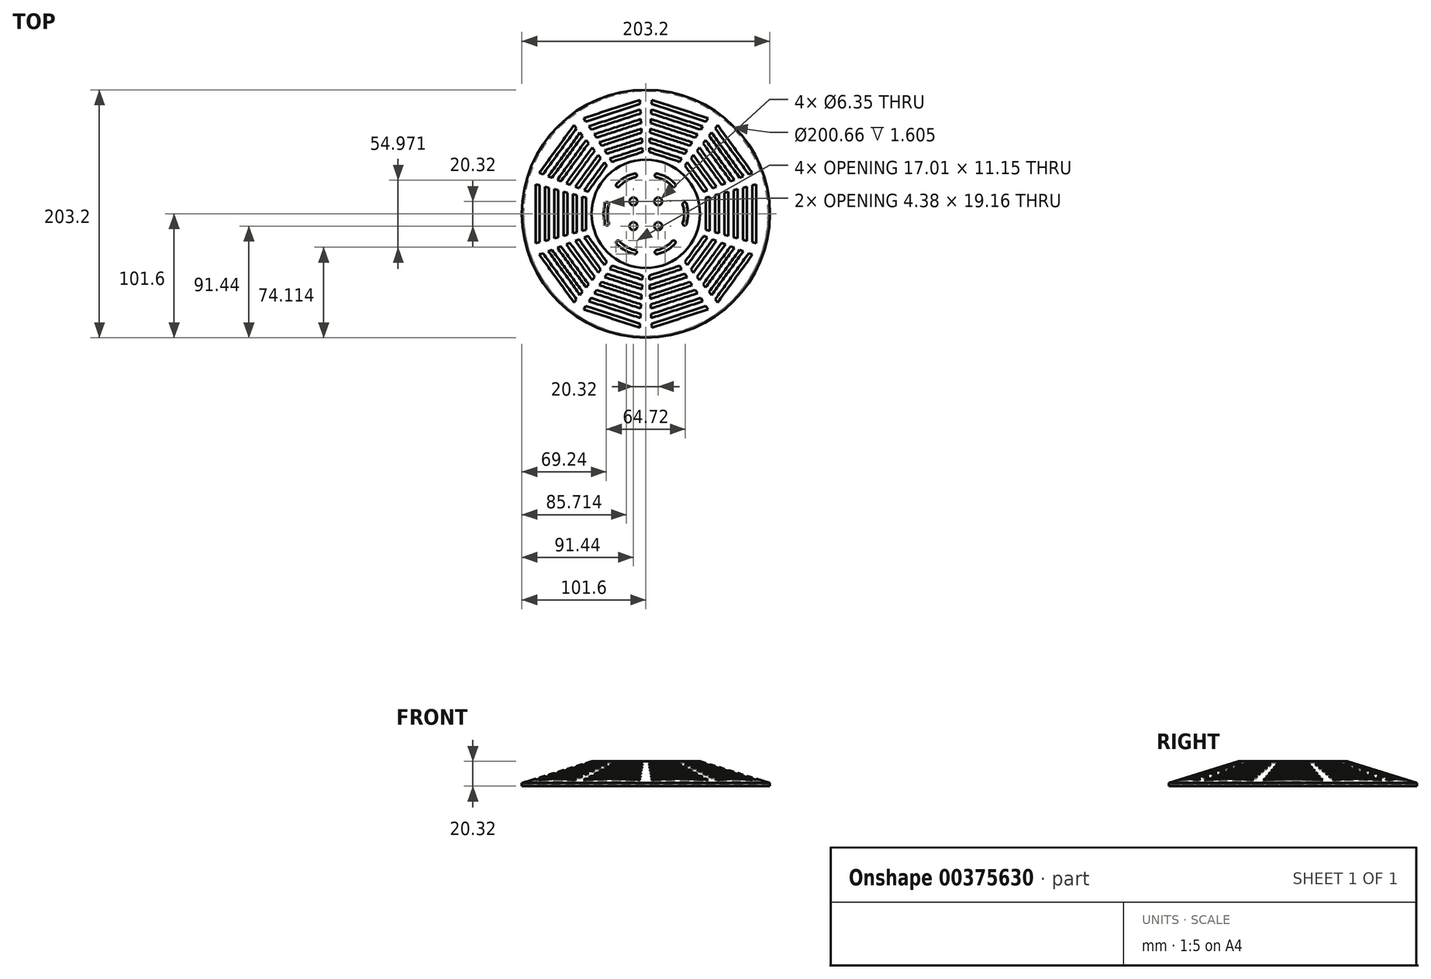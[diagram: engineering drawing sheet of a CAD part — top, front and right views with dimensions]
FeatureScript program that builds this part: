
annotation { "Feature Type Name" : "Feature", "Feature Type Description" : "" }
export const myFeature = defineFeature(function(context is Context, id is Id, definition is map)
    precondition{}
    {
        {
            var Q0;
            Q0=qCreatedBy(makeId("Front.planeOp"),FACE);
            var sketch = newSketch(context, id + "F0", { "sketchPlane" : qUnion([Q0])});
            skLineSegment(sketch, "E0", {"start": v(0, 0) * mm, "end": v(0, 20.32) * mm});
            skLineSegment(sketch, "E1", {"start": v(0, 20.32) * mm, "end": v(44.45, 20.32) * mm});
            skLineSegment(sketch, "E2", {"start": v(44.45, 20.32) * mm, "end": v(101.6, 2.54) * mm});
            skLineSegment(sketch, "E3", {"start": v(101.6, 2.54) * mm, "end": v(101.6, 0) * mm});
            skLineSegment(sketch, "E4", {"start": v(101.6, 0) * mm, "end": v(0, 0) * mm});
            skSolve(sketch);
        }
        {
            var Q0;
            Q0=makeQuery(id+"F0.imprint","IMPRINT",FACE,{"disambiguationData":[TD([[makeQuery(id+"F0.imprint","IMPRINT",EDGE,{"derivedFrom":sQuery(id+"F0.wireOp",EDGE,"E0")}),-1.0]])]});
            var Q1;
            Q1=sQuery(id+"F0.wireOp",EDGE,"E0");
            revolve(context, id + "F1", {"entities" : qUnion([Q0]), "axis" : qUnion([Q1]), "revolveType" : RevolveType.FULL});
        }
        {
            var Q0;
            Q0=makeQuery(id+"F1.opRevolve","SWEPT_FACE",FACE,{"disambiguationData":[OSD([sQuery(id+"F0.wireOp",EDGE,"E4")])]});
            shell(context, id + "F2", {"entities" : qUnion([Q0]), "thickness" : 1.27 * mm});
        }
        {
            var Q0;
            Q0=makeQuery(id+"F1.opRevolve","SWEPT_FACE",FACE,{"disambiguationData":[OSD([sQuery(id+"F0.wireOp",EDGE,"E1")])]});
            var sketch = newSketch(context, id + "F3", { "sketchPlane" : qUnion([Q0])});
            skArc(sketch, "E5", {"start": v(-30.23, 7.53) * mm, "mid": v(-31.38, 0) * mm, "end": v(-30.23, -7.53) * mm});
            skArc(sketch, "E6.0", {"start": v(-33.27, 8.47) * mm, "mid": v(-34.55, 0) * mm, "end": v(-33.27, -8.47) * mm});
            skArc(sketch, "E7", {"start": v(-33.27, -8.47) * mm, "mid": v(-31.28, -9.52) * mm, "end": v(-30.23, -7.53) * mm});
            skArc(sketch, "E8", {"start": v(-30.23, 7.53) * mm, "mid": v(-31.28, 9.52) * mm, "end": v(-33.27, 8.47) * mm});
            skSolve(sketch);
        }
        {
            var Q0;
            Q0=makeQuery(id+"F3.imprint","IMPRINT",FACE,{"disambiguationData":[TD([[makeQuery(id+"F3.imprint","IMPRINT",EDGE,{"derivedFrom":sQuery(id+"F3.wireOp",EDGE,"E5")}),-1.0]])]});
            extrude(context, id + "F4", {"entities" : qUnion([Q0]), "endBound" : BoundingType.THROUGH_ALL, "oppositeDirection" : true, "depth" : 25.4 * mm});
        }
        {
            var Q0;
            Q0=makeQuery(id+"F4.opExtrude","SWEPT_BODY",BODY,{"disambiguationData":[OSD([sQuery(id+"F3.wireOp",EDGE,"E5"),sQuery(id+"F3.wireOp",EDGE,"E6.0"),sQuery(id+"F3.wireOp",EDGE,"E7"),sQuery(id+"F3.wireOp",EDGE,"E8")])]});
            var Q1;
            Q1=makeQuery(id+"F1.opRevolve","SWEPT_EDGE",EDGE,{"disambiguationData":[OSD([sQuery(id+"F0.wireOp",EDGE,"E2"),sQuery(id+"F0.wireOp",EDGE,"E3")])]});
            circularPattern(context, id + "F5", {"entities" : qUnion([Q0]), "axis" : qUnion([Q1]), "angle" : 360 * degree, "instanceCount" : 6, "equalSpace" : true});
        }
        {
            var Q0;
            Q0=makeQuery(id+"F4.opExtrude","SWEPT_BODY",BODY,{"disambiguationData":[OSD([sQuery(id+"F3.wireOp",EDGE,"E5"),sQuery(id+"F3.wireOp",EDGE,"E6.0"),sQuery(id+"F3.wireOp",EDGE,"E7"),sQuery(id+"F3.wireOp",EDGE,"E8")])]});
            var Q1;
            Q1=makeQuery(id+"F5.opPattern","COPY",BODY,{"derivedFrom":makeQuery(id+"F4.opExtrude","SWEPT_BODY",BODY,{"disambiguationData":[OSD([sQuery(id+"F3.wireOp",EDGE,"E5"),sQuery(id+"F3.wireOp",EDGE,"E6.0"),sQuery(id+"F3.wireOp",EDGE,"E7"),sQuery(id+"F3.wireOp",EDGE,"E8")])]}),"instanceName":"1"});
            var Q2;
            Q2=makeQuery(id+"F5.opPattern","COPY",BODY,{"derivedFrom":makeQuery(id+"F4.opExtrude","SWEPT_BODY",BODY,{"disambiguationData":[OSD([sQuery(id+"F3.wireOp",EDGE,"E5"),sQuery(id+"F3.wireOp",EDGE,"E6.0"),sQuery(id+"F3.wireOp",EDGE,"E7"),sQuery(id+"F3.wireOp",EDGE,"E8")])]}),"instanceName":"2"});
            var Q3;
            Q3=makeQuery(id+"F5.opPattern","COPY",BODY,{"derivedFrom":makeQuery(id+"F4.opExtrude","SWEPT_BODY",BODY,{"disambiguationData":[OSD([sQuery(id+"F3.wireOp",EDGE,"E5"),sQuery(id+"F3.wireOp",EDGE,"E6.0"),sQuery(id+"F3.wireOp",EDGE,"E7"),sQuery(id+"F3.wireOp",EDGE,"E8")])]}),"instanceName":"3"});
            var Q4;
            Q4=makeQuery(id+"F5.opPattern","COPY",BODY,{"derivedFrom":makeQuery(id+"F4.opExtrude","SWEPT_BODY",BODY,{"disambiguationData":[OSD([sQuery(id+"F3.wireOp",EDGE,"E5"),sQuery(id+"F3.wireOp",EDGE,"E6.0"),sQuery(id+"F3.wireOp",EDGE,"E7"),sQuery(id+"F3.wireOp",EDGE,"E8")])]}),"instanceName":"4"});
            var Q5;
            Q5=makeQuery(id+"F5.opPattern","COPY",BODY,{"derivedFrom":makeQuery(id+"F4.opExtrude","SWEPT_BODY",BODY,{"disambiguationData":[OSD([sQuery(id+"F3.wireOp",EDGE,"E5"),sQuery(id+"F3.wireOp",EDGE,"E6.0"),sQuery(id+"F3.wireOp",EDGE,"E7"),sQuery(id+"F3.wireOp",EDGE,"E8")])]}),"instanceName":"5"});
            var Q6;
            Q6=makeQuery(id+"F1.opRevolve","SWEPT_BODY",BODY,{"disambiguationData":[OSD([sQuery(id+"F0.wireOp",EDGE,"E0"),sQuery(id+"F0.wireOp",EDGE,"E1"),sQuery(id+"F0.wireOp",EDGE,"E2"),sQuery(id+"F0.wireOp",EDGE,"E3"),sQuery(id+"F0.wireOp",EDGE,"E4")])]});
            booleanBodies(context, id + "F6", {"operationType" : BooleanOperationType.SUBTRACTION, "tools" : qUnion([Q0, Q1, Q2, Q3, Q4, Q5]), "targets" : qUnion([Q6])});
        }
        {
            var Q0;
            Q0=makeQuery(id+"F1.opRevolve","SWEPT_FACE",FACE,{"disambiguationData":[OSD([sQuery(id+"F0.wireOp",EDGE,"E1")])]});
            var sketch = newSketch(context, id + "F7", { "sketchPlane" : qUnion([Q0])});
            skLineSegment(sketch, "E9", {"start": v(0, 0) * mm, "end": v(-98.14, 26.3) * mm});
            skLineSegment(sketch, "E10", {"start": v(0, 0) * mm, "end": v(-98.14, -26.3) * mm});
            skLineSegment(sketch, "E11", {"start": v(-49.07, -13.15) * mm, "end": v(-49.07, 13.15) * mm});
            skLineSegment(sketch, "E12", {"start": v(-52.24, -14) * mm, "end": v(-52.24, 14) * mm});
            skLineSegment(sketch, "E13", {"start": v(-56.69, -15.19) * mm, "end": v(-56.69, 15.19) * mm});
            skLineSegment(sketch, "E14", {"start": v(-59.86, -16.04) * mm, "end": v(-59.86, 16.04) * mm});
            skLineSegment(sketch, "E15", {"start": v(-64.3, -17.23) * mm, "end": v(-64.3, 17.23) * mm});
            skLineSegment(sketch, "E16", {"start": v(-67.48, -18.08) * mm, "end": v(-67.48, 18.08) * mm});
            skLineSegment(sketch, "E17", {"start": v(-71.93, -19.27) * mm, "end": v(-71.93, 19.27) * mm});
            skLineSegment(sketch, "E18", {"start": v(-75.1, -20.12) * mm, "end": v(-75.1, 20.12) * mm});
            skLineSegment(sketch, "E19", {"start": v(-79.55, -21.32) * mm, "end": v(-79.55, 21.32) * mm});
            skLineSegment(sketch, "E20", {"start": v(-82.72, -22.17) * mm, "end": v(-82.72, 22.17) * mm});
            skLineSegment(sketch, "E21", {"start": v(-87.17, -23.36) * mm, "end": v(-87.17, 23.36) * mm});
            skLineSegment(sketch, "E22", {"start": v(-90.34, -24.2) * mm, "end": v(-90.34, 24.2) * mm});
            skSolve(sketch);
        }
        {
            var Q0;
            {var subQ1=sQuery(id+"F7.wireOp",EDGE,"E19");Q0=makeQuery(id+"F7.imprint","IMPRINT",FACE,{"disambiguationData":[TD([[makeQuery(id+"F7.imprint","IMPRINT",EDGE,{"derivedFrom":subQ1}),1.0]])]});}
            var Q1;
            {var subQ1=sQuery(id+"F7.wireOp",EDGE,"E17");Q1=makeQuery(id+"F7.imprint","IMPRINT",FACE,{"disambiguationData":[TD([[makeQuery(id+"F7.imprint","IMPRINT",EDGE,{"derivedFrom":subQ1}),1.0]])]});}
            var Q2;
            {var subQ1=sQuery(id+"F7.wireOp",EDGE,"E15");Q2=makeQuery(id+"F7.imprint","IMPRINT",FACE,{"disambiguationData":[TD([[makeQuery(id+"F7.imprint","IMPRINT",EDGE,{"derivedFrom":subQ1}),1.0]])]});}
            var Q3;
            {var subQ1=sQuery(id+"F7.wireOp",EDGE,"E13");Q3=makeQuery(id+"F7.imprint","IMPRINT",FACE,{"disambiguationData":[TD([[makeQuery(id+"F7.imprint","IMPRINT",EDGE,{"derivedFrom":subQ1}),1.0]])]});}
            var Q4;
            {var subQ1=sQuery(id+"F7.wireOp",EDGE,"E11");Q4=makeQuery(id+"F7.imprint","IMPRINT",FACE,{"disambiguationData":[TD([[makeQuery(id+"F7.imprint","IMPRINT",EDGE,{"derivedFrom":subQ1}),1.0]])]});}
            var Q5;
            {var subQ1=sQuery(id+"F7.wireOp",EDGE,"E21");Q5=makeQuery(id+"F7.imprint","IMPRINT",FACE,{"disambiguationData":[TD([[makeQuery(id+"F7.imprint","IMPRINT",EDGE,{"derivedFrom":subQ1}),1.0]])]});}
            extrude(context, id + "F8", {"entities" : qUnion([Q0, Q1, Q2, Q3, Q4, Q5]), "oppositeDirection" : true, "depth" : 25.4 * mm});
        }
        {
            var Q0;
            Q0=makeQuery(id+"F8.opExtrude","SWEPT_BODY",BODY,{"disambiguationData":[OSD([sQuery(id+"F7.wireOp",EDGE,"E9"),sQuery(id+"F7.wireOp",EDGE,"E10"),sQuery(id+"F7.wireOp",EDGE,"E21"),sQuery(id+"F7.wireOp",EDGE,"E22")])]});
            var Q1;
            Q1=makeQuery(id+"F8.opExtrude","SWEPT_BODY",BODY,{"disambiguationData":[OSD([sQuery(id+"F7.wireOp",EDGE,"E9"),sQuery(id+"F7.wireOp",EDGE,"E10"),sQuery(id+"F7.wireOp",EDGE,"E19"),sQuery(id+"F7.wireOp",EDGE,"E20")])]});
            var Q2;
            Q2=makeQuery(id+"F8.opExtrude","SWEPT_BODY",BODY,{"disambiguationData":[OSD([sQuery(id+"F7.wireOp",EDGE,"E9"),sQuery(id+"F7.wireOp",EDGE,"E10"),sQuery(id+"F7.wireOp",EDGE,"E17"),sQuery(id+"F7.wireOp",EDGE,"E18")])]});
            var Q3;
            Q3=makeQuery(id+"F8.opExtrude","SWEPT_BODY",BODY,{"disambiguationData":[OSD([sQuery(id+"F7.wireOp",EDGE,"E9"),sQuery(id+"F7.wireOp",EDGE,"E10"),sQuery(id+"F7.wireOp",EDGE,"E15"),sQuery(id+"F7.wireOp",EDGE,"E16")])]});
            var Q4;
            Q4=makeQuery(id+"F8.opExtrude","SWEPT_BODY",BODY,{"disambiguationData":[OSD([sQuery(id+"F7.wireOp",EDGE,"E9"),sQuery(id+"F7.wireOp",EDGE,"E10"),sQuery(id+"F7.wireOp",EDGE,"E13"),sQuery(id+"F7.wireOp",EDGE,"E14")])]});
            var Q5;
            Q5=makeQuery(id+"F8.opExtrude","SWEPT_BODY",BODY,{"disambiguationData":[OSD([sQuery(id+"F7.wireOp",EDGE,"E9"),sQuery(id+"F7.wireOp",EDGE,"E10"),sQuery(id+"F7.wireOp",EDGE,"E11"),sQuery(id+"F7.wireOp",EDGE,"E12")])]});
            var Q6;
            Q6=makeQuery(id+"F1.opRevolve","SWEPT_EDGE",EDGE,{"disambiguationData":[OSD([sQuery(id+"F0.wireOp",EDGE,"E2"),sQuery(id+"F0.wireOp",EDGE,"E3")])]});
            circularPattern(context, id + "F9", {"entities" : qUnion([Q0, Q1, Q2, Q3, Q4, Q5]), "axis" : qUnion([Q6]), "angle" : 360 * degree, "instanceCount" : 10, "equalSpace" : true});
        }
        {
            var Q0;
            Q0=makeQuery(id+"F8.opExtrude","SWEPT_BODY",BODY,{"disambiguationData":[OSD([sQuery(id+"F7.wireOp",EDGE,"E9"),sQuery(id+"F7.wireOp",EDGE,"E10"),sQuery(id+"F7.wireOp",EDGE,"E21"),sQuery(id+"F7.wireOp",EDGE,"E22")])]});
            var Q1;
            Q1=makeQuery(id+"F8.opExtrude","SWEPT_BODY",BODY,{"disambiguationData":[OSD([sQuery(id+"F7.wireOp",EDGE,"E9"),sQuery(id+"F7.wireOp",EDGE,"E10"),sQuery(id+"F7.wireOp",EDGE,"E11"),sQuery(id+"F7.wireOp",EDGE,"E12")])]});
            var Q2;
            Q2=makeQuery(id+"F8.opExtrude","SWEPT_BODY",BODY,{"disambiguationData":[OSD([sQuery(id+"F7.wireOp",EDGE,"E9"),sQuery(id+"F7.wireOp",EDGE,"E10"),sQuery(id+"F7.wireOp",EDGE,"E13"),sQuery(id+"F7.wireOp",EDGE,"E14")])]});
            var Q3;
            Q3=makeQuery(id+"F8.opExtrude","SWEPT_BODY",BODY,{"disambiguationData":[OSD([sQuery(id+"F7.wireOp",EDGE,"E9"),sQuery(id+"F7.wireOp",EDGE,"E10"),sQuery(id+"F7.wireOp",EDGE,"E15"),sQuery(id+"F7.wireOp",EDGE,"E16")])]});
            var Q4;
            Q4=makeQuery(id+"F8.opExtrude","SWEPT_BODY",BODY,{"disambiguationData":[OSD([sQuery(id+"F7.wireOp",EDGE,"E9"),sQuery(id+"F7.wireOp",EDGE,"E10"),sQuery(id+"F7.wireOp",EDGE,"E17"),sQuery(id+"F7.wireOp",EDGE,"E18")])]});
            var Q5;
            Q5=makeQuery(id+"F8.opExtrude","SWEPT_BODY",BODY,{"disambiguationData":[OSD([sQuery(id+"F7.wireOp",EDGE,"E9"),sQuery(id+"F7.wireOp",EDGE,"E10"),sQuery(id+"F7.wireOp",EDGE,"E19"),sQuery(id+"F7.wireOp",EDGE,"E20")])]});
            var Q6;
            Q6=makeQuery(id+"F9.opPattern","COPY",BODY,{"derivedFrom":makeQuery(id+"F8.opExtrude","SWEPT_BODY",BODY,{"disambiguationData":[OSD([sQuery(id+"F7.wireOp",EDGE,"E9"),sQuery(id+"F7.wireOp",EDGE,"E10"),sQuery(id+"F7.wireOp",EDGE,"E21"),sQuery(id+"F7.wireOp",EDGE,"E22")])]}),"instanceName":"1"});
            var Q7;
            Q7=makeQuery(id+"F9.opPattern","COPY",BODY,{"derivedFrom":makeQuery(id+"F8.opExtrude","SWEPT_BODY",BODY,{"disambiguationData":[OSD([sQuery(id+"F7.wireOp",EDGE,"E9"),sQuery(id+"F7.wireOp",EDGE,"E10"),sQuery(id+"F7.wireOp",EDGE,"E11"),sQuery(id+"F7.wireOp",EDGE,"E12")])]}),"instanceName":"1"});
            var Q8;
            Q8=makeQuery(id+"F9.opPattern","COPY",BODY,{"derivedFrom":makeQuery(id+"F8.opExtrude","SWEPT_BODY",BODY,{"disambiguationData":[OSD([sQuery(id+"F7.wireOp",EDGE,"E9"),sQuery(id+"F7.wireOp",EDGE,"E10"),sQuery(id+"F7.wireOp",EDGE,"E13"),sQuery(id+"F7.wireOp",EDGE,"E14")])]}),"instanceName":"1"});
            var Q9;
            Q9=makeQuery(id+"F9.opPattern","COPY",BODY,{"derivedFrom":makeQuery(id+"F8.opExtrude","SWEPT_BODY",BODY,{"disambiguationData":[OSD([sQuery(id+"F7.wireOp",EDGE,"E9"),sQuery(id+"F7.wireOp",EDGE,"E10"),sQuery(id+"F7.wireOp",EDGE,"E15"),sQuery(id+"F7.wireOp",EDGE,"E16")])]}),"instanceName":"1"});
            var Q10;
            Q10=makeQuery(id+"F9.opPattern","COPY",BODY,{"derivedFrom":makeQuery(id+"F8.opExtrude","SWEPT_BODY",BODY,{"disambiguationData":[OSD([sQuery(id+"F7.wireOp",EDGE,"E9"),sQuery(id+"F7.wireOp",EDGE,"E10"),sQuery(id+"F7.wireOp",EDGE,"E17"),sQuery(id+"F7.wireOp",EDGE,"E18")])]}),"instanceName":"1"});
            var Q11;
            Q11=makeQuery(id+"F9.opPattern","COPY",BODY,{"derivedFrom":makeQuery(id+"F8.opExtrude","SWEPT_BODY",BODY,{"disambiguationData":[OSD([sQuery(id+"F7.wireOp",EDGE,"E9"),sQuery(id+"F7.wireOp",EDGE,"E10"),sQuery(id+"F7.wireOp",EDGE,"E19"),sQuery(id+"F7.wireOp",EDGE,"E20")])]}),"instanceName":"1"});
            var Q12;
            Q12=makeQuery(id+"F9.opPattern","COPY",BODY,{"derivedFrom":makeQuery(id+"F8.opExtrude","SWEPT_BODY",BODY,{"disambiguationData":[OSD([sQuery(id+"F7.wireOp",EDGE,"E9"),sQuery(id+"F7.wireOp",EDGE,"E10"),sQuery(id+"F7.wireOp",EDGE,"E21"),sQuery(id+"F7.wireOp",EDGE,"E22")])]}),"instanceName":"2"});
            var Q13;
            Q13=makeQuery(id+"F9.opPattern","COPY",BODY,{"derivedFrom":makeQuery(id+"F8.opExtrude","SWEPT_BODY",BODY,{"disambiguationData":[OSD([sQuery(id+"F7.wireOp",EDGE,"E9"),sQuery(id+"F7.wireOp",EDGE,"E10"),sQuery(id+"F7.wireOp",EDGE,"E11"),sQuery(id+"F7.wireOp",EDGE,"E12")])]}),"instanceName":"2"});
            var Q14;
            Q14=makeQuery(id+"F9.opPattern","COPY",BODY,{"derivedFrom":makeQuery(id+"F8.opExtrude","SWEPT_BODY",BODY,{"disambiguationData":[OSD([sQuery(id+"F7.wireOp",EDGE,"E9"),sQuery(id+"F7.wireOp",EDGE,"E10"),sQuery(id+"F7.wireOp",EDGE,"E13"),sQuery(id+"F7.wireOp",EDGE,"E14")])]}),"instanceName":"2"});
            var Q15;
            Q15=makeQuery(id+"F9.opPattern","COPY",BODY,{"derivedFrom":makeQuery(id+"F8.opExtrude","SWEPT_BODY",BODY,{"disambiguationData":[OSD([sQuery(id+"F7.wireOp",EDGE,"E9"),sQuery(id+"F7.wireOp",EDGE,"E10"),sQuery(id+"F7.wireOp",EDGE,"E15"),sQuery(id+"F7.wireOp",EDGE,"E16")])]}),"instanceName":"2"});
            var Q16;
            Q16=makeQuery(id+"F9.opPattern","COPY",BODY,{"derivedFrom":makeQuery(id+"F8.opExtrude","SWEPT_BODY",BODY,{"disambiguationData":[OSD([sQuery(id+"F7.wireOp",EDGE,"E9"),sQuery(id+"F7.wireOp",EDGE,"E10"),sQuery(id+"F7.wireOp",EDGE,"E17"),sQuery(id+"F7.wireOp",EDGE,"E18")])]}),"instanceName":"2"});
            var Q17;
            Q17=makeQuery(id+"F9.opPattern","COPY",BODY,{"derivedFrom":makeQuery(id+"F8.opExtrude","SWEPT_BODY",BODY,{"disambiguationData":[OSD([sQuery(id+"F7.wireOp",EDGE,"E9"),sQuery(id+"F7.wireOp",EDGE,"E10"),sQuery(id+"F7.wireOp",EDGE,"E19"),sQuery(id+"F7.wireOp",EDGE,"E20")])]}),"instanceName":"2"});
            var Q18;
            Q18=makeQuery(id+"F9.opPattern","COPY",BODY,{"derivedFrom":makeQuery(id+"F8.opExtrude","SWEPT_BODY",BODY,{"disambiguationData":[OSD([sQuery(id+"F7.wireOp",EDGE,"E9"),sQuery(id+"F7.wireOp",EDGE,"E10"),sQuery(id+"F7.wireOp",EDGE,"E21"),sQuery(id+"F7.wireOp",EDGE,"E22")])]}),"instanceName":"3"});
            var Q19;
            Q19=makeQuery(id+"F9.opPattern","COPY",BODY,{"derivedFrom":makeQuery(id+"F8.opExtrude","SWEPT_BODY",BODY,{"disambiguationData":[OSD([sQuery(id+"F7.wireOp",EDGE,"E9"),sQuery(id+"F7.wireOp",EDGE,"E10"),sQuery(id+"F7.wireOp",EDGE,"E11"),sQuery(id+"F7.wireOp",EDGE,"E12")])]}),"instanceName":"3"});
            var Q20;
            Q20=makeQuery(id+"F9.opPattern","COPY",BODY,{"derivedFrom":makeQuery(id+"F8.opExtrude","SWEPT_BODY",BODY,{"disambiguationData":[OSD([sQuery(id+"F7.wireOp",EDGE,"E9"),sQuery(id+"F7.wireOp",EDGE,"E10"),sQuery(id+"F7.wireOp",EDGE,"E13"),sQuery(id+"F7.wireOp",EDGE,"E14")])]}),"instanceName":"3"});
            var Q21;
            Q21=makeQuery(id+"F9.opPattern","COPY",BODY,{"derivedFrom":makeQuery(id+"F8.opExtrude","SWEPT_BODY",BODY,{"disambiguationData":[OSD([sQuery(id+"F7.wireOp",EDGE,"E9"),sQuery(id+"F7.wireOp",EDGE,"E10"),sQuery(id+"F7.wireOp",EDGE,"E15"),sQuery(id+"F7.wireOp",EDGE,"E16")])]}),"instanceName":"3"});
            var Q22;
            Q22=makeQuery(id+"F9.opPattern","COPY",BODY,{"derivedFrom":makeQuery(id+"F8.opExtrude","SWEPT_BODY",BODY,{"disambiguationData":[OSD([sQuery(id+"F7.wireOp",EDGE,"E9"),sQuery(id+"F7.wireOp",EDGE,"E10"),sQuery(id+"F7.wireOp",EDGE,"E17"),sQuery(id+"F7.wireOp",EDGE,"E18")])]}),"instanceName":"3"});
            var Q23;
            Q23=makeQuery(id+"F9.opPattern","COPY",BODY,{"derivedFrom":makeQuery(id+"F8.opExtrude","SWEPT_BODY",BODY,{"disambiguationData":[OSD([sQuery(id+"F7.wireOp",EDGE,"E9"),sQuery(id+"F7.wireOp",EDGE,"E10"),sQuery(id+"F7.wireOp",EDGE,"E19"),sQuery(id+"F7.wireOp",EDGE,"E20")])]}),"instanceName":"3"});
            var Q24;
            Q24=makeQuery(id+"F9.opPattern","COPY",BODY,{"derivedFrom":makeQuery(id+"F8.opExtrude","SWEPT_BODY",BODY,{"disambiguationData":[OSD([sQuery(id+"F7.wireOp",EDGE,"E9"),sQuery(id+"F7.wireOp",EDGE,"E10"),sQuery(id+"F7.wireOp",EDGE,"E21"),sQuery(id+"F7.wireOp",EDGE,"E22")])]}),"instanceName":"4"});
            var Q25;
            Q25=makeQuery(id+"F9.opPattern","COPY",BODY,{"derivedFrom":makeQuery(id+"F8.opExtrude","SWEPT_BODY",BODY,{"disambiguationData":[OSD([sQuery(id+"F7.wireOp",EDGE,"E9"),sQuery(id+"F7.wireOp",EDGE,"E10"),sQuery(id+"F7.wireOp",EDGE,"E11"),sQuery(id+"F7.wireOp",EDGE,"E12")])]}),"instanceName":"4"});
            var Q26;
            Q26=makeQuery(id+"F9.opPattern","COPY",BODY,{"derivedFrom":makeQuery(id+"F8.opExtrude","SWEPT_BODY",BODY,{"disambiguationData":[OSD([sQuery(id+"F7.wireOp",EDGE,"E9"),sQuery(id+"F7.wireOp",EDGE,"E10"),sQuery(id+"F7.wireOp",EDGE,"E13"),sQuery(id+"F7.wireOp",EDGE,"E14")])]}),"instanceName":"4"});
            var Q27;
            Q27=makeQuery(id+"F9.opPattern","COPY",BODY,{"derivedFrom":makeQuery(id+"F8.opExtrude","SWEPT_BODY",BODY,{"disambiguationData":[OSD([sQuery(id+"F7.wireOp",EDGE,"E9"),sQuery(id+"F7.wireOp",EDGE,"E10"),sQuery(id+"F7.wireOp",EDGE,"E15"),sQuery(id+"F7.wireOp",EDGE,"E16")])]}),"instanceName":"4"});
            var Q28;
            Q28=makeQuery(id+"F9.opPattern","COPY",BODY,{"derivedFrom":makeQuery(id+"F8.opExtrude","SWEPT_BODY",BODY,{"disambiguationData":[OSD([sQuery(id+"F7.wireOp",EDGE,"E9"),sQuery(id+"F7.wireOp",EDGE,"E10"),sQuery(id+"F7.wireOp",EDGE,"E17"),sQuery(id+"F7.wireOp",EDGE,"E18")])]}),"instanceName":"4"});
            var Q29;
            Q29=makeQuery(id+"F9.opPattern","COPY",BODY,{"derivedFrom":makeQuery(id+"F8.opExtrude","SWEPT_BODY",BODY,{"disambiguationData":[OSD([sQuery(id+"F7.wireOp",EDGE,"E9"),sQuery(id+"F7.wireOp",EDGE,"E10"),sQuery(id+"F7.wireOp",EDGE,"E19"),sQuery(id+"F7.wireOp",EDGE,"E20")])]}),"instanceName":"4"});
            var Q30;
            Q30=makeQuery(id+"F9.opPattern","COPY",BODY,{"derivedFrom":makeQuery(id+"F8.opExtrude","SWEPT_BODY",BODY,{"disambiguationData":[OSD([sQuery(id+"F7.wireOp",EDGE,"E9"),sQuery(id+"F7.wireOp",EDGE,"E10"),sQuery(id+"F7.wireOp",EDGE,"E21"),sQuery(id+"F7.wireOp",EDGE,"E22")])]}),"instanceName":"5"});
            var Q31;
            Q31=makeQuery(id+"F9.opPattern","COPY",BODY,{"derivedFrom":makeQuery(id+"F8.opExtrude","SWEPT_BODY",BODY,{"disambiguationData":[OSD([sQuery(id+"F7.wireOp",EDGE,"E9"),sQuery(id+"F7.wireOp",EDGE,"E10"),sQuery(id+"F7.wireOp",EDGE,"E11"),sQuery(id+"F7.wireOp",EDGE,"E12")])]}),"instanceName":"5"});
            var Q32;
            Q32=makeQuery(id+"F9.opPattern","COPY",BODY,{"derivedFrom":makeQuery(id+"F8.opExtrude","SWEPT_BODY",BODY,{"disambiguationData":[OSD([sQuery(id+"F7.wireOp",EDGE,"E9"),sQuery(id+"F7.wireOp",EDGE,"E10"),sQuery(id+"F7.wireOp",EDGE,"E13"),sQuery(id+"F7.wireOp",EDGE,"E14")])]}),"instanceName":"5"});
            var Q33;
            Q33=makeQuery(id+"F9.opPattern","COPY",BODY,{"derivedFrom":makeQuery(id+"F8.opExtrude","SWEPT_BODY",BODY,{"disambiguationData":[OSD([sQuery(id+"F7.wireOp",EDGE,"E9"),sQuery(id+"F7.wireOp",EDGE,"E10"),sQuery(id+"F7.wireOp",EDGE,"E15"),sQuery(id+"F7.wireOp",EDGE,"E16")])]}),"instanceName":"5"});
            var Q34;
            Q34=makeQuery(id+"F9.opPattern","COPY",BODY,{"derivedFrom":makeQuery(id+"F8.opExtrude","SWEPT_BODY",BODY,{"disambiguationData":[OSD([sQuery(id+"F7.wireOp",EDGE,"E9"),sQuery(id+"F7.wireOp",EDGE,"E10"),sQuery(id+"F7.wireOp",EDGE,"E17"),sQuery(id+"F7.wireOp",EDGE,"E18")])]}),"instanceName":"5"});
            var Q35;
            Q35=makeQuery(id+"F9.opPattern","COPY",BODY,{"derivedFrom":makeQuery(id+"F8.opExtrude","SWEPT_BODY",BODY,{"disambiguationData":[OSD([sQuery(id+"F7.wireOp",EDGE,"E9"),sQuery(id+"F7.wireOp",EDGE,"E10"),sQuery(id+"F7.wireOp",EDGE,"E19"),sQuery(id+"F7.wireOp",EDGE,"E20")])]}),"instanceName":"5"});
            var Q36;
            Q36=makeQuery(id+"F9.opPattern","COPY",BODY,{"derivedFrom":makeQuery(id+"F8.opExtrude","SWEPT_BODY",BODY,{"disambiguationData":[OSD([sQuery(id+"F7.wireOp",EDGE,"E9"),sQuery(id+"F7.wireOp",EDGE,"E10"),sQuery(id+"F7.wireOp",EDGE,"E21"),sQuery(id+"F7.wireOp",EDGE,"E22")])]}),"instanceName":"6"});
            var Q37;
            Q37=makeQuery(id+"F9.opPattern","COPY",BODY,{"derivedFrom":makeQuery(id+"F8.opExtrude","SWEPT_BODY",BODY,{"disambiguationData":[OSD([sQuery(id+"F7.wireOp",EDGE,"E9"),sQuery(id+"F7.wireOp",EDGE,"E10"),sQuery(id+"F7.wireOp",EDGE,"E11"),sQuery(id+"F7.wireOp",EDGE,"E12")])]}),"instanceName":"6"});
            var Q38;
            Q38=makeQuery(id+"F9.opPattern","COPY",BODY,{"derivedFrom":makeQuery(id+"F8.opExtrude","SWEPT_BODY",BODY,{"disambiguationData":[OSD([sQuery(id+"F7.wireOp",EDGE,"E9"),sQuery(id+"F7.wireOp",EDGE,"E10"),sQuery(id+"F7.wireOp",EDGE,"E13"),sQuery(id+"F7.wireOp",EDGE,"E14")])]}),"instanceName":"6"});
            var Q39;
            Q39=makeQuery(id+"F9.opPattern","COPY",BODY,{"derivedFrom":makeQuery(id+"F8.opExtrude","SWEPT_BODY",BODY,{"disambiguationData":[OSD([sQuery(id+"F7.wireOp",EDGE,"E9"),sQuery(id+"F7.wireOp",EDGE,"E10"),sQuery(id+"F7.wireOp",EDGE,"E15"),sQuery(id+"F7.wireOp",EDGE,"E16")])]}),"instanceName":"6"});
            var Q40;
            Q40=makeQuery(id+"F9.opPattern","COPY",BODY,{"derivedFrom":makeQuery(id+"F8.opExtrude","SWEPT_BODY",BODY,{"disambiguationData":[OSD([sQuery(id+"F7.wireOp",EDGE,"E9"),sQuery(id+"F7.wireOp",EDGE,"E10"),sQuery(id+"F7.wireOp",EDGE,"E17"),sQuery(id+"F7.wireOp",EDGE,"E18")])]}),"instanceName":"6"});
            var Q41;
            Q41=makeQuery(id+"F9.opPattern","COPY",BODY,{"derivedFrom":makeQuery(id+"F8.opExtrude","SWEPT_BODY",BODY,{"disambiguationData":[OSD([sQuery(id+"F7.wireOp",EDGE,"E9"),sQuery(id+"F7.wireOp",EDGE,"E10"),sQuery(id+"F7.wireOp",EDGE,"E19"),sQuery(id+"F7.wireOp",EDGE,"E20")])]}),"instanceName":"6"});
            var Q42;
            Q42=makeQuery(id+"F9.opPattern","COPY",BODY,{"derivedFrom":makeQuery(id+"F8.opExtrude","SWEPT_BODY",BODY,{"disambiguationData":[OSD([sQuery(id+"F7.wireOp",EDGE,"E9"),sQuery(id+"F7.wireOp",EDGE,"E10"),sQuery(id+"F7.wireOp",EDGE,"E21"),sQuery(id+"F7.wireOp",EDGE,"E22")])]}),"instanceName":"7"});
            var Q43;
            Q43=makeQuery(id+"F9.opPattern","COPY",BODY,{"derivedFrom":makeQuery(id+"F8.opExtrude","SWEPT_BODY",BODY,{"disambiguationData":[OSD([sQuery(id+"F7.wireOp",EDGE,"E9"),sQuery(id+"F7.wireOp",EDGE,"E10"),sQuery(id+"F7.wireOp",EDGE,"E11"),sQuery(id+"F7.wireOp",EDGE,"E12")])]}),"instanceName":"7"});
            var Q44;
            Q44=makeQuery(id+"F9.opPattern","COPY",BODY,{"derivedFrom":makeQuery(id+"F8.opExtrude","SWEPT_BODY",BODY,{"disambiguationData":[OSD([sQuery(id+"F7.wireOp",EDGE,"E9"),sQuery(id+"F7.wireOp",EDGE,"E10"),sQuery(id+"F7.wireOp",EDGE,"E13"),sQuery(id+"F7.wireOp",EDGE,"E14")])]}),"instanceName":"7"});
            var Q45;
            Q45=makeQuery(id+"F9.opPattern","COPY",BODY,{"derivedFrom":makeQuery(id+"F8.opExtrude","SWEPT_BODY",BODY,{"disambiguationData":[OSD([sQuery(id+"F7.wireOp",EDGE,"E9"),sQuery(id+"F7.wireOp",EDGE,"E10"),sQuery(id+"F7.wireOp",EDGE,"E15"),sQuery(id+"F7.wireOp",EDGE,"E16")])]}),"instanceName":"7"});
            var Q46;
            Q46=makeQuery(id+"F9.opPattern","COPY",BODY,{"derivedFrom":makeQuery(id+"F8.opExtrude","SWEPT_BODY",BODY,{"disambiguationData":[OSD([sQuery(id+"F7.wireOp",EDGE,"E9"),sQuery(id+"F7.wireOp",EDGE,"E10"),sQuery(id+"F7.wireOp",EDGE,"E17"),sQuery(id+"F7.wireOp",EDGE,"E18")])]}),"instanceName":"7"});
            var Q47;
            Q47=makeQuery(id+"F9.opPattern","COPY",BODY,{"derivedFrom":makeQuery(id+"F8.opExtrude","SWEPT_BODY",BODY,{"disambiguationData":[OSD([sQuery(id+"F7.wireOp",EDGE,"E9"),sQuery(id+"F7.wireOp",EDGE,"E10"),sQuery(id+"F7.wireOp",EDGE,"E19"),sQuery(id+"F7.wireOp",EDGE,"E20")])]}),"instanceName":"7"});
            var Q48;
            Q48=makeQuery(id+"F9.opPattern","COPY",BODY,{"derivedFrom":makeQuery(id+"F8.opExtrude","SWEPT_BODY",BODY,{"disambiguationData":[OSD([sQuery(id+"F7.wireOp",EDGE,"E9"),sQuery(id+"F7.wireOp",EDGE,"E10"),sQuery(id+"F7.wireOp",EDGE,"E21"),sQuery(id+"F7.wireOp",EDGE,"E22")])]}),"instanceName":"8"});
            var Q49;
            Q49=makeQuery(id+"F9.opPattern","COPY",BODY,{"derivedFrom":makeQuery(id+"F8.opExtrude","SWEPT_BODY",BODY,{"disambiguationData":[OSD([sQuery(id+"F7.wireOp",EDGE,"E9"),sQuery(id+"F7.wireOp",EDGE,"E10"),sQuery(id+"F7.wireOp",EDGE,"E11"),sQuery(id+"F7.wireOp",EDGE,"E12")])]}),"instanceName":"8"});
            var Q50;
            Q50=makeQuery(id+"F9.opPattern","COPY",BODY,{"derivedFrom":makeQuery(id+"F8.opExtrude","SWEPT_BODY",BODY,{"disambiguationData":[OSD([sQuery(id+"F7.wireOp",EDGE,"E9"),sQuery(id+"F7.wireOp",EDGE,"E10"),sQuery(id+"F7.wireOp",EDGE,"E13"),sQuery(id+"F7.wireOp",EDGE,"E14")])]}),"instanceName":"8"});
            var Q51;
            Q51=makeQuery(id+"F9.opPattern","COPY",BODY,{"derivedFrom":makeQuery(id+"F8.opExtrude","SWEPT_BODY",BODY,{"disambiguationData":[OSD([sQuery(id+"F7.wireOp",EDGE,"E9"),sQuery(id+"F7.wireOp",EDGE,"E10"),sQuery(id+"F7.wireOp",EDGE,"E15"),sQuery(id+"F7.wireOp",EDGE,"E16")])]}),"instanceName":"8"});
            var Q52;
            Q52=makeQuery(id+"F9.opPattern","COPY",BODY,{"derivedFrom":makeQuery(id+"F8.opExtrude","SWEPT_BODY",BODY,{"disambiguationData":[OSD([sQuery(id+"F7.wireOp",EDGE,"E9"),sQuery(id+"F7.wireOp",EDGE,"E10"),sQuery(id+"F7.wireOp",EDGE,"E17"),sQuery(id+"F7.wireOp",EDGE,"E18")])]}),"instanceName":"8"});
            var Q53;
            Q53=makeQuery(id+"F9.opPattern","COPY",BODY,{"derivedFrom":makeQuery(id+"F8.opExtrude","SWEPT_BODY",BODY,{"disambiguationData":[OSD([sQuery(id+"F7.wireOp",EDGE,"E9"),sQuery(id+"F7.wireOp",EDGE,"E10"),sQuery(id+"F7.wireOp",EDGE,"E19"),sQuery(id+"F7.wireOp",EDGE,"E20")])]}),"instanceName":"8"});
            var Q54;
            Q54=makeQuery(id+"F9.opPattern","COPY",BODY,{"derivedFrom":makeQuery(id+"F8.opExtrude","SWEPT_BODY",BODY,{"disambiguationData":[OSD([sQuery(id+"F7.wireOp",EDGE,"E9"),sQuery(id+"F7.wireOp",EDGE,"E10"),sQuery(id+"F7.wireOp",EDGE,"E21"),sQuery(id+"F7.wireOp",EDGE,"E22")])]}),"instanceName":"9"});
            var Q55;
            Q55=makeQuery(id+"F9.opPattern","COPY",BODY,{"derivedFrom":makeQuery(id+"F8.opExtrude","SWEPT_BODY",BODY,{"disambiguationData":[OSD([sQuery(id+"F7.wireOp",EDGE,"E9"),sQuery(id+"F7.wireOp",EDGE,"E10"),sQuery(id+"F7.wireOp",EDGE,"E11"),sQuery(id+"F7.wireOp",EDGE,"E12")])]}),"instanceName":"9"});
            var Q56;
            Q56=makeQuery(id+"F9.opPattern","COPY",BODY,{"derivedFrom":makeQuery(id+"F8.opExtrude","SWEPT_BODY",BODY,{"disambiguationData":[OSD([sQuery(id+"F7.wireOp",EDGE,"E9"),sQuery(id+"F7.wireOp",EDGE,"E10"),sQuery(id+"F7.wireOp",EDGE,"E13"),sQuery(id+"F7.wireOp",EDGE,"E14")])]}),"instanceName":"9"});
            var Q57;
            Q57=makeQuery(id+"F9.opPattern","COPY",BODY,{"derivedFrom":makeQuery(id+"F8.opExtrude","SWEPT_BODY",BODY,{"disambiguationData":[OSD([sQuery(id+"F7.wireOp",EDGE,"E9"),sQuery(id+"F7.wireOp",EDGE,"E10"),sQuery(id+"F7.wireOp",EDGE,"E15"),sQuery(id+"F7.wireOp",EDGE,"E16")])]}),"instanceName":"9"});
            var Q58;
            Q58=makeQuery(id+"F9.opPattern","COPY",BODY,{"derivedFrom":makeQuery(id+"F8.opExtrude","SWEPT_BODY",BODY,{"disambiguationData":[OSD([sQuery(id+"F7.wireOp",EDGE,"E9"),sQuery(id+"F7.wireOp",EDGE,"E10"),sQuery(id+"F7.wireOp",EDGE,"E17"),sQuery(id+"F7.wireOp",EDGE,"E18")])]}),"instanceName":"9"});
            var Q59;
            Q59=makeQuery(id+"F9.opPattern","COPY",BODY,{"derivedFrom":makeQuery(id+"F8.opExtrude","SWEPT_BODY",BODY,{"disambiguationData":[OSD([sQuery(id+"F7.wireOp",EDGE,"E9"),sQuery(id+"F7.wireOp",EDGE,"E10"),sQuery(id+"F7.wireOp",EDGE,"E19"),sQuery(id+"F7.wireOp",EDGE,"E20")])]}),"instanceName":"9"});
            var Q60;
            Q60=makeQuery(id+"F1.opRevolve","SWEPT_BODY",BODY,{"disambiguationData":[OSD([sQuery(id+"F0.wireOp",EDGE,"E0"),sQuery(id+"F0.wireOp",EDGE,"E1"),sQuery(id+"F0.wireOp",EDGE,"E2"),sQuery(id+"F0.wireOp",EDGE,"E3"),sQuery(id+"F0.wireOp",EDGE,"E4")])]});
            booleanBodies(context, id + "F10", {"operationType" : BooleanOperationType.SUBTRACTION, "tools" : qUnion([Q0, Q1, Q2, Q3, Q4, Q5, Q6, Q7, Q8, Q9, Q10, Q11, Q12, Q13, Q14, Q15, Q16, Q17, Q18, Q19, Q20, Q21, Q22, Q23, Q24, Q25, Q26, Q27, Q28, Q29, Q30, Q31, Q32, Q33, Q34, Q35, Q36, Q37, Q38, Q39, Q40, Q41, Q42, Q43, Q44, Q45, Q46, Q47, Q48, Q49, Q50, Q51, Q52, Q53, Q54, Q55, Q56, Q57, Q58, Q59]), "targets" : qUnion([Q60])});
        }
        {
            var Q0;
            Q0=makeQuery(id+"F1.opRevolve","SWEPT_FACE",FACE,{"disambiguationData":[OSD([sQuery(id+"F0.wireOp",EDGE,"E1")])]});
            var sketch = newSketch(context, id + "F11", { "sketchPlane" : qUnion([Q0])});
            skCircle(sketch, "E23", {"center": v(-10.16, -10.16) * mm, "radius": 3.18 * mm});
            skCircle(sketch, "E24", {"center": v(-10.16, 10.16) * mm, "radius": 3.18 * mm});
            skCircle(sketch, "E25", {"center": v(10.16, -10.16) * mm, "radius": 3.18 * mm});
            skCircle(sketch, "E26", {"center": v(10.16, 10.16) * mm, "radius": 3.18 * mm});
            skSolve(sketch);
        }
        {
            var Q0;
            {Q0=qUnion([makeQuery(id+"F11.imprint","IMPRINT",FACE,{"disambiguationData":[TD([[makeQuery(id+"F11.imprint","IMPRINT",EDGE,{"derivedFrom":sQuery(id+"F11.wireOp",EDGE,"E23")}),1.0]])]}),makeQuery(id+"F11.imprint","IMPRINT",FACE,{"disambiguationData":[TD([[makeQuery(id+"F11.imprint","IMPRINT",EDGE,{"derivedFrom":sQuery(id+"F11.wireOp",EDGE,"E24")}),1.0]])]}),makeQuery(id+"F11.imprint","IMPRINT",FACE,{"disambiguationData":[TD([[makeQuery(id+"F11.imprint","IMPRINT",EDGE,{"derivedFrom":sQuery(id+"F11.wireOp",EDGE,"E25")}),1.0]])]}),makeQuery(id+"F11.imprint","IMPRINT",FACE,{"disambiguationData":[TD([[makeQuery(id+"F11.imprint","IMPRINT",EDGE,{"derivedFrom":sQuery(id+"F11.wireOp",EDGE,"E26")}),1.0]])]})]);}
            extrude(context, id + "F12", {"entities" : qUnion([Q0]), "operationType" : NewBodyOperationType.REMOVE, "endBound" : BoundingType.THROUGH_ALL, "oppositeDirection" : true, "depth" : 25.4 * mm});
        }
        {
            var Q0;
            Q0=makeQuery(id+"F2.opShell","OFFSET_FACE",FACE,{"disambiguationData":[OSD([sQuery(id+"F0.wireOp",EDGE,"E1")])]});
            var Q1;
            Q1=makeQuery(id+"F2.opShell","OFFSET_FACE",FACE,{"disambiguationData":[OSD([sQuery(id+"F0.wireOp",EDGE,"E2")])]});
            shell(context, id + "F13", {"entities" : qUnion([Q0, Q1]), "thickness" : 1.27 * mm});
        }
    });
